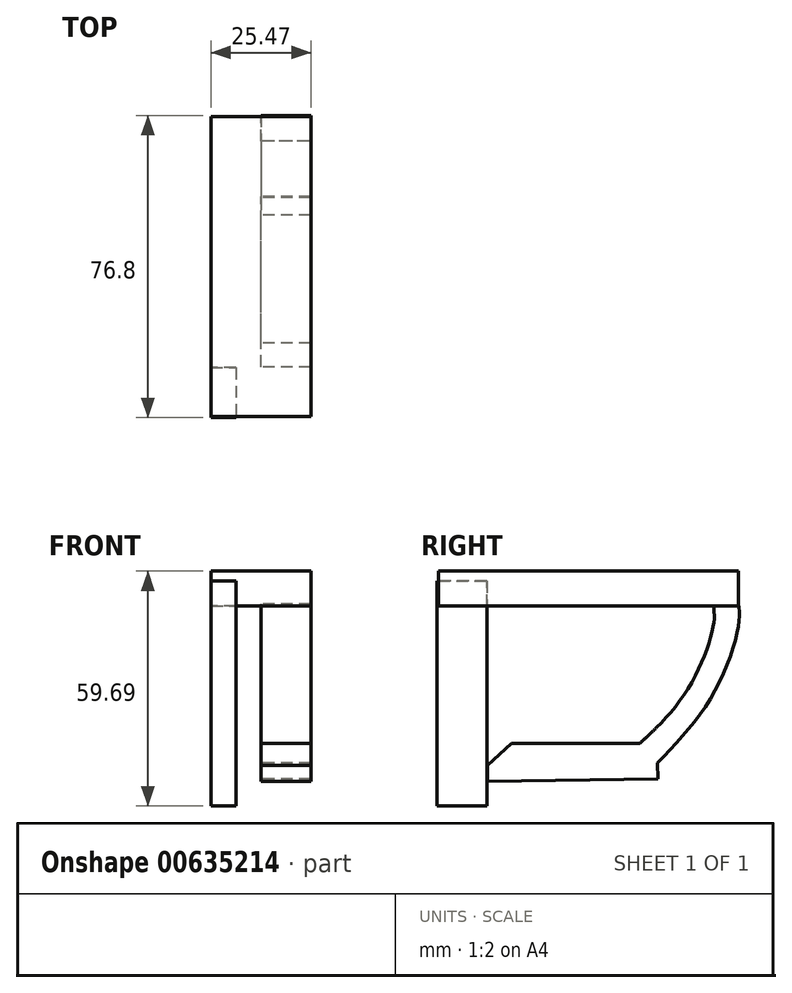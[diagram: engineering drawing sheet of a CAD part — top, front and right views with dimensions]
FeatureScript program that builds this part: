
annotation { "Feature Type Name" : "Feature", "Feature Type Description" : "" }
export const myFeature = defineFeature(function(context is Context, id is Id, definition is map)
    precondition{}
    {
        {
            var Q0;
            Q0=qCreatedBy(makeId("Right.planeOp"),FACE);
            var sketch = newSketch(context, id + "F0", { "sketchPlane" : qUnion([Q0])});
            skLineSegment(sketch, "E0.bottom", {"start": v(6.35, 28.57) * mm, "end": v(-6.35, 28.57) * mm});
            skLineSegment(sketch, "E0.top", {"start": v(6.35, -28.58) * mm, "end": v(-6.35, -28.58) * mm});
            skLineSegment(sketch, "E0.left", {"start": v(6.35, 28.58) * mm, "end": v(6.35, -28.58) * mm});
            skLineSegment(sketch, "E0.right", {"start": v(-6.35, 28.57) * mm, "end": v(-6.35, -28.58) * mm});
            skPoint(sketch, "E0.middle", {"position": v(0, 0) * mm});
            skSolve(sketch);
        }
        {
            var Q0;
            Q0 = qSketchRegion(id + "F0", true);
            extrude(context, id + "F1", {"entities" : qUnion([Q0]), "oppositeDirection" : true, "depth" : 6.35 * mm, "offsetDistance" : 25.4 * mm});
        }
        {
            var Q0;
            Q0=qCreatedBy(makeId("Top.planeOp"),FACE);
            cPlane(context, id + "F2", {"entities" : qUnion([Q0]), "cplaneType" : CPlaneType.OFFSET, "offset" : 28.57 * mm, "width" : 152.4 * mm, "height" : 152.4 * mm});
        }
        {
            var Q0;
            Q0=qCreatedBy(id+"F2.planeOp",FACE);
            var sketch = newSketch(context, id + "F3", { "sketchPlane" : qUnion([Q0])});
            skLineSegment(sketch, "E1.bottom", {"start": v(-6.28, -6.05) * mm, "end": v(19.12, -6.05) * mm});
            skLineSegment(sketch, "E1.top", {"start": v(-6.28, 70.15) * mm, "end": v(19.12, 70.15) * mm});
            skLineSegment(sketch, "E1.left", {"start": v(-6.28, -6.05) * mm, "end": v(-6.28, 70.15) * mm});
            skLineSegment(sketch, "E1.right", {"start": v(19.12, -6.05) * mm, "end": v(19.12, 70.15) * mm});
            skSolve(sketch);
        }
        {
            var Q0;
            Q0=makeQuery(id+"F3.imprint","IMPRINT",FACE,{"disambiguationData":[TD([[makeQuery(id+"F3.imprint","IMPRINT",EDGE,{"derivedFrom":sQuery(id+"F3.wireOp",EDGE,"E1.bottom")}),1.0]])]});
            extrude(context, id + "F4", {"entities" : qUnion([Q0]), "operationType" : NewBodyOperationType.ADD, "oppositeDirection" : true, "depth" : 6.35 * mm, "offsetDistance" : 25.4 * mm, "hasSecondDirection" : true, "secondDirectionOppositeDirection" : false, "secondDirectionDepth" : 2.54 * mm});
        }
        {
            var Q0;
            Q0=qCreatedBy(makeId("Right.planeOp"),FACE);
            cPlane(context, id + "F5", {"entities" : qUnion([Q0]), "cplaneType" : CPlaneType.OFFSET, "offset" : 6.35 * mm, "width" : 152.4 * mm, "height" : 152.4 * mm});
        }
        {
            var Q0;
            Q0=qCreatedBy(id+"F5.planeOp",FACE);
            var sketch = newSketch(context, id + "F6", { "sketchPlane" : qUnion([Q0])});
            skFitSpline(sketch, "E2", {"points": [v(70.26, 22.84) * mm, v(70.26, 17.6) * mm, v(63.86, 0) * mm, v(49.6, -17.6) * mm, v(34.19, -33.02) * mm], "startDerivative": vector(3.37, -31.13) * mm, "endDerivative": vector(-53.04, -52.44) * mm});
            skFitSpline(sketch, "E3", {"points": [v(63.86, 22.26) * mm, v(63.86, 17.31) * mm, v(56.59, 0) * mm, v(42.91, -14.7) * mm, v(32.15, -24.88) * mm], "startDerivative": vector(3.59, -27.81) * mm, "endDerivative": vector(-39.84, -38.36) * mm});
            skLineSegment(sketch, "E4", {"start": v(63.86, 22.26) * mm, "end": v(70.26, 22.84) * mm});
            skLineSegment(sketch, "E5", {"start": v(49.39, -8.63) * mm, "end": v(49.6, -8.63) * mm});
            skLineSegment(sketch, "E6", {"start": v(6.46, -18.18) * mm, "end": v(49.6, -17.6) * mm});
            skLineSegment(sketch, "E7", {"start": v(6.46, -18.18) * mm, "end": v(12.57, -12.66) * mm});
            skLineSegment(sketch, "E8", {"start": v(12.57, -12.66) * mm, "end": v(45.14, -12.66) * mm});
            skLineSegment(sketch, "E9", {"start": v(6.46, -18.18) * mm, "end": v(6.52, -22.26) * mm});
            skLineSegment(sketch, "E10", {"start": v(6.52, -22.26) * mm, "end": v(49.8, -21.68) * mm});
            skLineSegment(sketch, "E11", {"start": v(49.8, -21.68) * mm, "end": v(49.6, -17.6) * mm});
            skSolve(sketch);
        }
        {
            var Q0;
            Q0 = qSketchRegion(id + "F6", true);
            extrude(context, id + "F7", {"entities" : qUnion([Q0]), "operationType" : NewBodyOperationType.ADD, "depth" : 12.7 * mm, "offsetDistance" : 25.4 * mm});
        }
    });
